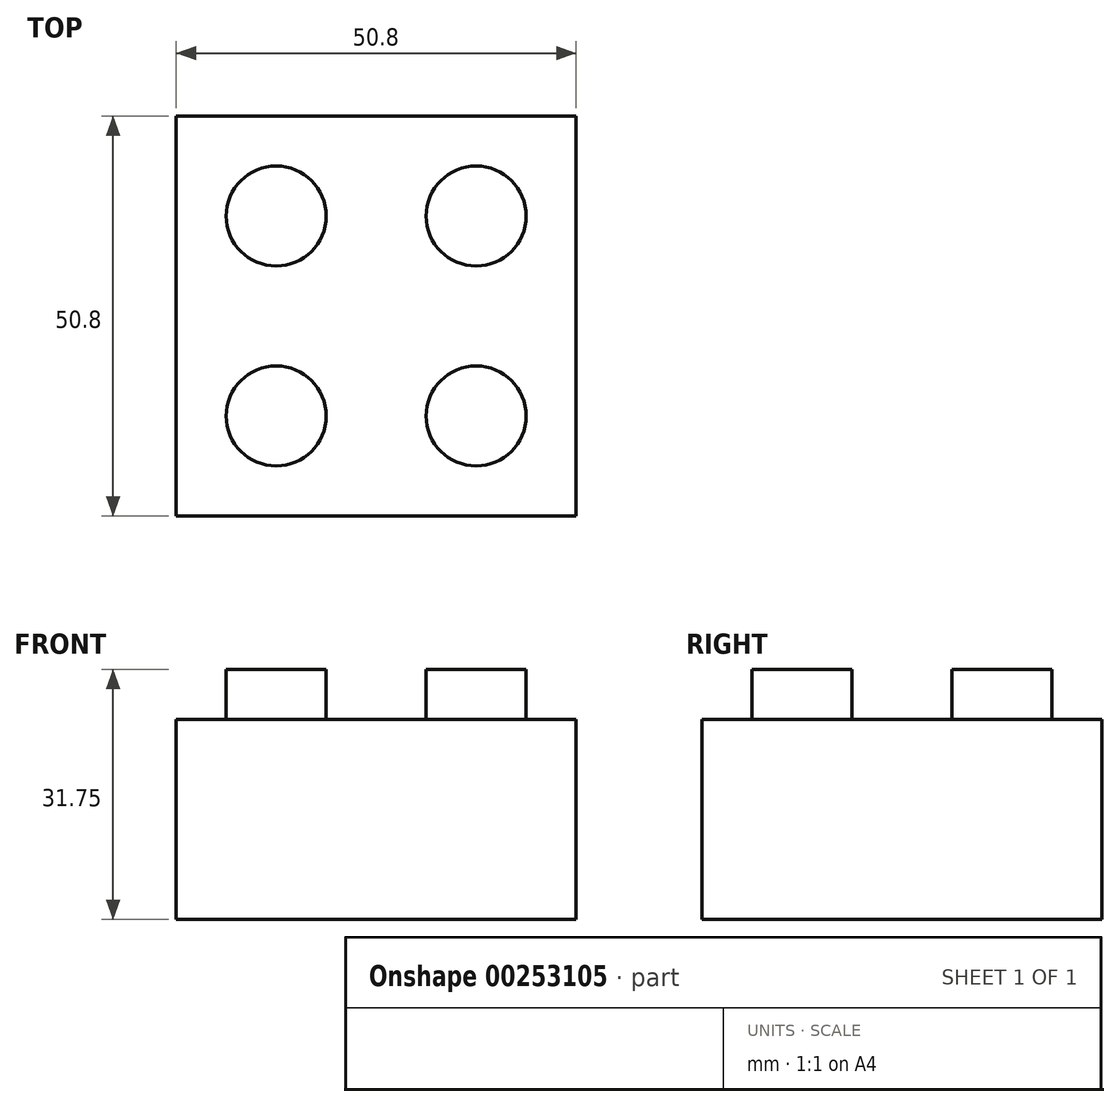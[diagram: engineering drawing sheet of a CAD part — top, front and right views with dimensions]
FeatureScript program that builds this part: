
annotation { "Feature Type Name" : "Feature", "Feature Type Description" : "" }
export const myFeature = defineFeature(function(context is Context, id is Id, definition is map)
    precondition{}
    {
        {
            var Q0;
            Q0=qCreatedBy(makeId("Top.planeOp"),FACE);
            var sketch = newSketch(context, id + "F0", { "sketchPlane" : qUnion([Q0])});
            skLineSegment(sketch, "E0.bottom", {"start": v(-9.56, 8.94) * mm, "end": v(41.24, 8.94) * mm});
            skLineSegment(sketch, "E0.top", {"start": v(-9.56, -41.86) * mm, "end": v(41.24, -41.86) * mm});
            skLineSegment(sketch, "E0.left", {"start": v(-9.56, 8.94) * mm, "end": v(-9.56, -41.86) * mm});
            skLineSegment(sketch, "E0.right", {"start": v(41.24, 8.94) * mm, "end": v(41.24, -41.86) * mm});
            skLineSegment(sketch, "E1", {"start": v(-9.56, 8.94) * mm, "end": v(-9.56, -3.76) * mm});
            skLineSegment(sketch, "E2", {"start": v(-9.56, 8.94) * mm, "end": v(3.14, 8.94) * mm});
            skCircle(sketch, "E3", {"center": v(3.14, -3.76) * mm, "radius": 6.35 * mm});
            skLineSegment(sketch, "E4", {"start": v(-9.56, -41.86) * mm, "end": v(-9.56, -29.16) * mm});
            skLineSegment(sketch, "E5", {"start": v(-9.56, -41.86) * mm, "end": v(3.14, -41.86) * mm});
            skLineSegment(sketch, "E6", {"start": v(28.54, 8.94) * mm, "end": v(41.24, 8.94) * mm});
            skLineSegment(sketch, "E7", {"start": v(41.24, 8.94) * mm, "end": v(41.24, -3.76) * mm});
            skLineSegment(sketch, "E8", {"start": v(41.24, -41.86) * mm, "end": v(41.24, -29.16) * mm});
            skLineSegment(sketch, "E9", {"start": v(41.24, -41.86) * mm, "end": v(28.54, -41.86) * mm});
            skCircle(sketch, "E10", {"center": v(3.14, -29.16) * mm, "radius": 6.35 * mm});
            skCircle(sketch, "E11", {"center": v(28.54, -3.76) * mm, "radius": 6.35 * mm});
            skCircle(sketch, "E12", {"center": v(28.54, -29.16) * mm, "radius": 6.35 * mm});
            skSolve(sketch);
        }
        {
            var Q0;
            Q0=makeQuery(id+"F0.imprint","IMPRINT",FACE,{"disambiguationData":[TD([[makeQuery(id+"F0.imprint","IMPRINT",EDGE,{"derivedFrom":sQuery(id+"F0.wireOp",EDGE,"E0.bottom")}),-1.0]])]});
            extrude(context, id + "F1", {"entities" : qUnion([Q0]), "depth" : 25.4 * mm});
        }
        {
            var Q0;
            Q0=makeQuery(id+"F0.imprint","IMPRINT",FACE,{"disambiguationData":[TD([[makeQuery(id+"F0.imprint","IMPRINT",EDGE,{"derivedFrom":sQuery(id+"F0.wireOp",EDGE,"E12")}),1.0]])]});
            var Q1;
            Q1=makeQuery(id+"F0.imprint","IMPRINT",FACE,{"disambiguationData":[TD([[makeQuery(id+"F0.imprint","IMPRINT",EDGE,{"derivedFrom":sQuery(id+"F0.wireOp",EDGE,"E3")}),1.0]])]});
            var Q2;
            Q2=makeQuery(id+"F0.imprint","IMPRINT",FACE,{"disambiguationData":[TD([[makeQuery(id+"F0.imprint","IMPRINT",EDGE,{"derivedFrom":sQuery(id+"F0.wireOp",EDGE,"E11")}),1.0]])]});
            var Q3;
            Q3=makeQuery(id+"F0.imprint","IMPRINT",FACE,{"disambiguationData":[TD([[makeQuery(id+"F0.imprint","IMPRINT",EDGE,{"derivedFrom":sQuery(id+"F0.wireOp",EDGE,"E10")}),1.0]])]});
            extrude(context, id + "F2", {"entities" : qUnion([Q0, Q1, Q2, Q3]), "operationType" : NewBodyOperationType.ADD, "depth" : 31.75 * mm});
        }
    });
